# Revit family: Electronics_Visual-TVs_ViewSonic_The-ViewSonicR-CDE6510-Series-Large-Form
name_source: partatom
category: Electrical Equipment
revit_build: Autodesk Revit 2015 (Build: 20140606_1530(x64)
units: mm (PartAtom-declared; Revit-internal decimal feet)

## types (1)
- CDE6510
    Assembly Code = D50
    BIMobject category = Visual - TVs
    BIMobject category code = electronics-visual-tvs
    BIMobject main category = Electronics
    BIMobject main category code = electronics
    BOSUseNativeGeometries = 1
    Brand url = https://www.viewsonic.com
    Covering Color = Plastic - Viewsonic - Black
    Description = he ViewSonic® CDE6510 is a 65’’ (64.5” viewable) 4K Ultra HD commercial display purpose-built to deliver eye-catching imagery for hotels, restaurants, retail, business, and more. With stunning 3840x2160 resolution, 350-nit high brightness, wide viewing angles, and dual 10W speakers, this display provides immersive, high-impact messaging wherever needed. An embedded Android SOC allows you to install Android apps for rich content broadcasting. In addition to HDMI, DVI, and VGA inputs to connect with various high definition devices, this display utilizes an integrated multi-core processor and 8GB of internal memory, allowing customers to playback multimedia content via USB without the need for a PC. To make life even easier, the bundled vController software offers easy maintenance and intuitive interfaces for remote management via a PC server or laptop, and its flicker-free and blue light filter technologies help provide a comfortable viewing environment.
    Design country = Taiwan
    Edition number = 1
    Keynote = V90
    Manufacturer = ViewSonic
    Manufacturer country = Taiwan
    Manufacturer name = ViewSonic
    Model = viewsonic_cde6510
    Product Guid = c63aa9d2-2c25-47cf-a022-f83b0a0e8042
    Product SKU = viewsonic_cde6510
    Product data url = https://bimobject.com
    Product family = Electronics
    Product group = Large Format Displays
    Product name = The ViewSonic® CDE6510 Series Large Format Displays
    Product url = https://www.viewsonic.com
    QR code = http://bimobject.com
    URL = www.viewsonic.com
    Youtube clip = https://www.youtube.com

## geometry (parser evidence)
native form markers: Sweep x3
no freeform markers — native parametric forms only
